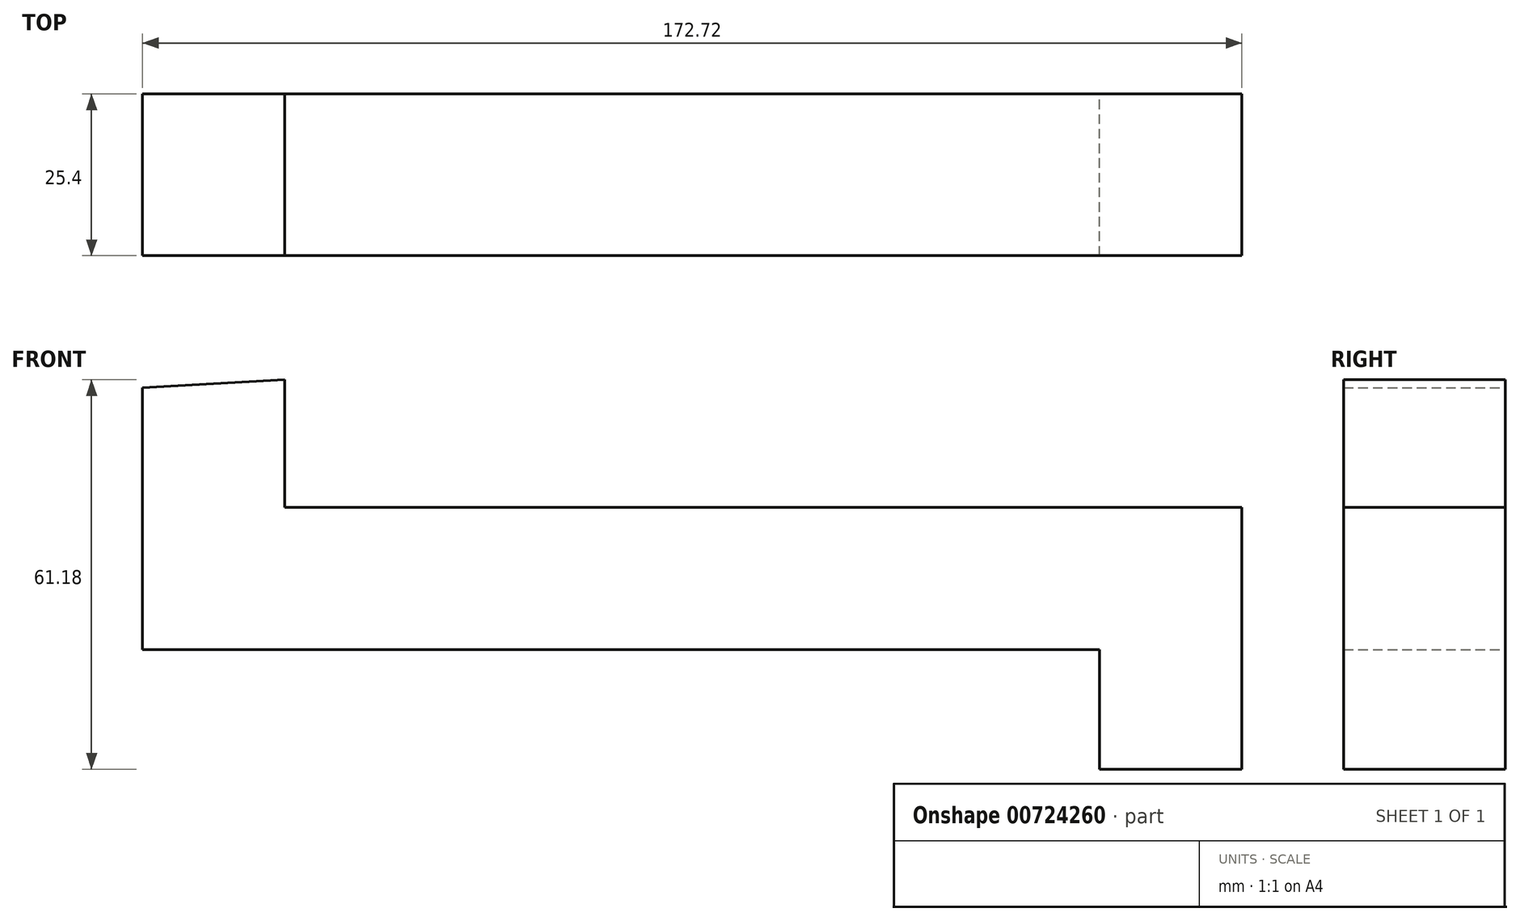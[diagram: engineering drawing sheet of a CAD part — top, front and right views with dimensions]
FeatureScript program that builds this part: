
annotation { "Feature Type Name" : "Feature", "Feature Type Description" : "" }
export const myFeature = defineFeature(function(context is Context, id is Id, definition is map)
    precondition{}
    {
        {
            var Q0;
            Q0=qCreatedBy(makeId("Front.planeOp"),FACE);
            var sketch = newSketch(context, id + "F0", { "sketchPlane" : qUnion([Q0])});
            skLineSegment(sketch, "E0", {"start": v(-66.87, 44.87) * mm, "end": v(-66.87, 3.72) * mm});
            skLineSegment(sketch, "E1", {"start": v(83.5, 3.72) * mm, "end": v(-66.87, 3.72) * mm});
            skLineSegment(sketch, "E2", {"start": v(83.5, 3.72) * mm, "end": v(83.5, -15.08) * mm});
            skLineSegment(sketch, "E3", {"start": v(105.85, -15.08) * mm, "end": v(83.5, -15.08) * mm});
            skLineSegment(sketch, "E4", {"start": v(105.85, 26.07) * mm, "end": v(105.85, -15.08) * mm});
            skLineSegment(sketch, "E5", {"start": v(-44.52, 26.07) * mm, "end": v(105.85, 26.07) * mm});
            skLineSegment(sketch, "E6", {"start": v(-44.52, 46.1) * mm, "end": v(-44.52, 26.07) * mm});
            skLineSegment(sketch, "E7", {"start": v(-44.52, 46.1) * mm, "end": v(-66.87, 44.87) * mm});
            skSolve(sketch);
        }
        {
            var Q0;
            Q0 = qSketchRegion(id + "F0", true);
            extrude(context, id + "F1", {"entities" : qUnion([Q0]), "depth" : 25.4 * mm, "offsetDistance" : 25.4 * mm});
        }
    });
